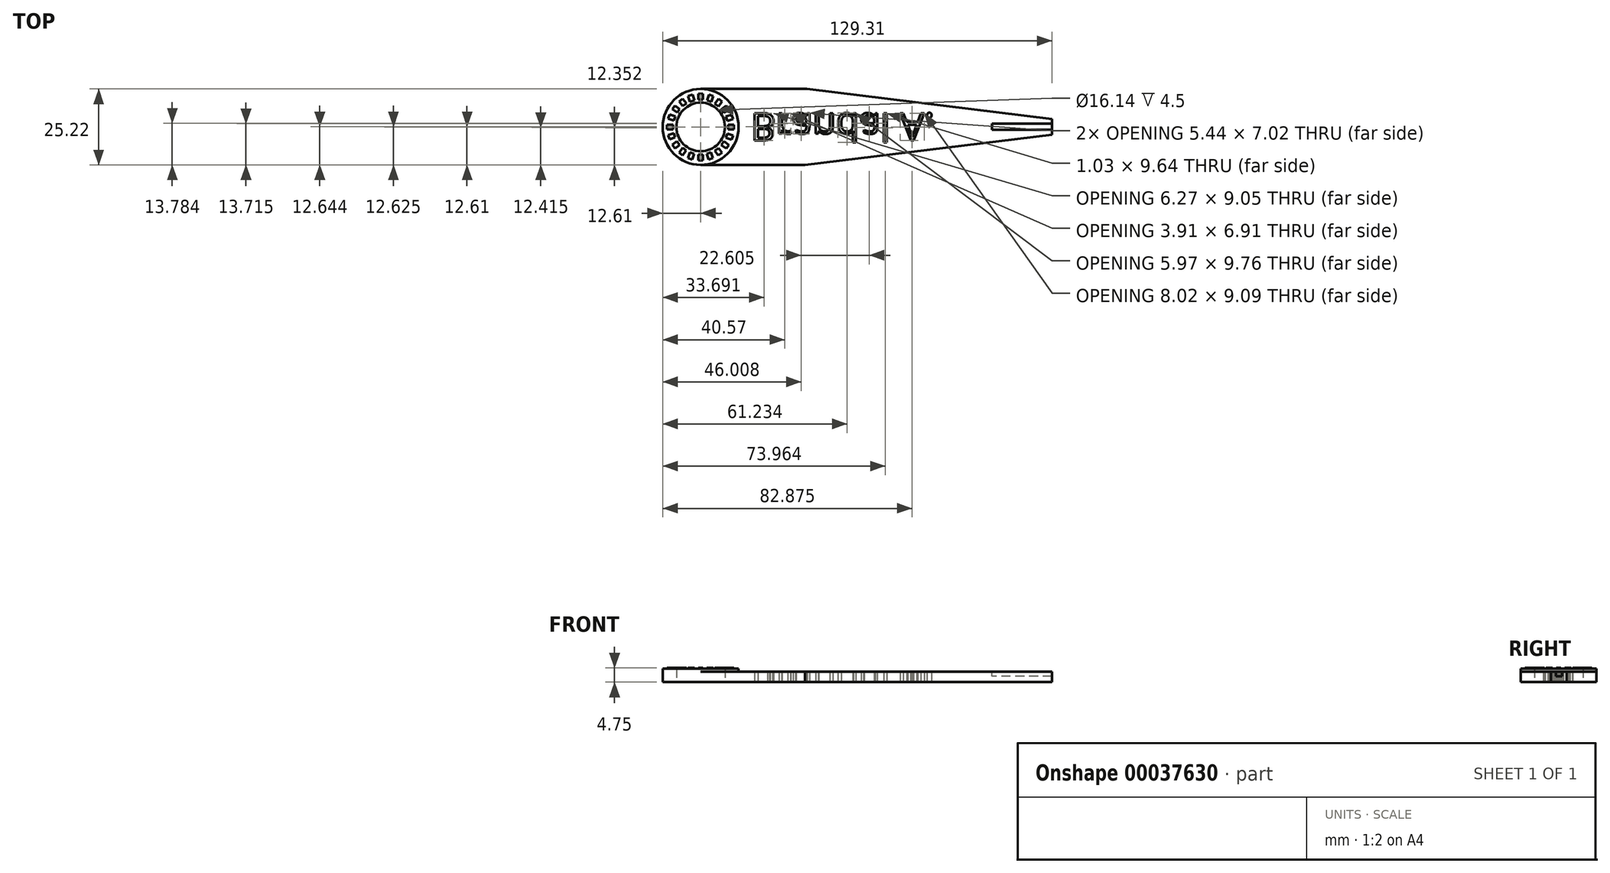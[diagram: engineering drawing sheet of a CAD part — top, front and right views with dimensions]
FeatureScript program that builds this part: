
annotation { "Feature Type Name" : "Feature", "Feature Type Description" : "" }
export const myFeature = defineFeature(function(context is Context, id is Id, definition is map)
    precondition{}
    {
        {
            var Q0;
            Q0=qCreatedBy(makeId("Top.planeOp"),FACE);
            var sketch = newSketch(context, id + "F0", { "sketchPlane" : qUnion([Q0])});
            skCircle(sketch, "E0", {"center": v(0, 0) * mm, "radius": 8.07 * mm});
            skArc(sketch, "E1", {"start": v(0, 12.6) * mm, "mid": v(-12.6, 0) * mm, "end": v(0, -12.6) * mm});
            skLineSegment(sketch, "E2", {"start": v(35.3, 12.6) * mm, "end": v(0, 12.6) * mm});
            skLineSegment(sketch, "E3", {"start": v(34.7, -12.6) * mm, "end": v(0, -12.6) * mm});
            skLineSegment(sketch, "E4", {"start": v(35.3, 12.6) * mm, "end": v(125.73, 12.6) * mm, "construction": true});
            skLineSegment(sketch, "E5", {"start": v(35.3, 12.6) * mm, "end": v(116.7, 2.62) * mm});
            skLineSegment(sketch, "E6.MirrorCS", {"start": v(34.7, -12.6) * mm, "end": v(116.7, -2.62) * mm});
            skLineSegment(sketch, "E7", {"start": v(116.7, 2.62) * mm, "end": v(116.7, -2.62) * mm});
            skSolve(sketch);
        }
        {
            var Q0;
            Q0=qSketchRegion(id+"F0",true);
            extrude(context, id + "F1", {"entities" : qUnion([Q0]), "depth" : 3.5 * mm});
        }
        {
            var Q0;
            Q0=makeQuery(id+"F1.opExtrude","CAP_FACE",FACE,{"disambiguationData":[OSD([sQuery(id+"F0.wireOp",EDGE,"E0"),sQuery(id+"F0.wireOp",EDGE,"E1"),sQuery(id+"F0.wireOp",EDGE,"E2"),sQuery(id+"F0.wireOp",EDGE,"E3"),sQuery(id+"F0.wireOp",EDGE,"E5"),sQuery(id+"F0.wireOp",EDGE,"E6.MirrorCS"),sQuery(id+"F0.wireOp",EDGE,"E7")])],"isStart":false});
            var sketch = newSketch(context, id + "F2", { "sketchPlane" : qUnion([Q0])});
            skCircle(sketch, "E8", {"center": v(0, 0) * mm, "radius": 8.07 * mm});
            skCircle(sketch, "E9", {"center": v(0, 0) * mm, "radius": 12.6 * mm});
            skSolve(sketch);
        }
        {
            var Q0;
            Q0=qSketchRegion(id+"F2",true);
            extrude(context, id + "F3", {"entities" : qUnion([Q0]), "operationType" : NewBodyOperationType.ADD, "depth" : 1 * mm});
        }
        {
            var Q0;
            Q0=makeQuery(id+"F3.opExtrude","CAP_FACE",FACE,{"disambiguationData":[OSD([sQuery(id+"F2.wireOp",EDGE,"E8"),sQuery(id+"F2.wireOp",EDGE,"E9")])],"isStart":false});
            var sketch = newSketch(context, id + "F4", { "sketchPlane" : qUnion([Q0])});
            skLineSegment(sketch, "E10.bottom", {"start": v(-0.75, 11.07) * mm, "end": v(0.75, 11.07) * mm});
            skLineSegment(sketch, "E10.top", {"start": v(-0.75, 9.07) * mm, "end": v(0.75, 9.07) * mm});
            skLineSegment(sketch, "E10.left", {"start": v(-0.75, 11.07) * mm, "end": v(-0.75, 9.07) * mm});
            skLineSegment(sketch, "E10.right", {"start": v(0.75, 11.07) * mm, "end": v(0.75, 9.07) * mm});
            skPoint(sketch, "E11", {"position": v(0, 8.07) * mm});
            skLineSegment(sketch, "E12.1.0", {"start": v(-4.14, 10.3) * mm, "end": v(-2.72, 10.77) * mm});
            skLineSegment(sketch, "E12.1.1", {"start": v(-4.14, 10.3) * mm, "end": v(-3.53, 8.4) * mm});
            skLineSegment(sketch, "E12.1.2", {"start": v(-3.53, 8.4) * mm, "end": v(-2.1, 8.87) * mm});
            skLineSegment(sketch, "E12.1.3", {"start": v(-2.72, 10.77) * mm, "end": v(-2.1, 8.87) * mm});
            skLineSegment(sketch, "E12.2.0", {"start": v(-7.14, 8.53) * mm, "end": v(-5.92, 9.4) * mm});
            skLineSegment(sketch, "E12.2.1", {"start": v(-7.14, 8.53) * mm, "end": v(-5.96, 6.9) * mm});
            skLineSegment(sketch, "E12.2.2", {"start": v(-5.96, 6.9) * mm, "end": v(-4.75, 7.8) * mm});
            skLineSegment(sketch, "E12.2.3", {"start": v(-5.92, 9.4) * mm, "end": v(-4.75, 7.8) * mm});
            skLineSegment(sketch, "E12.3.0", {"start": v(-9.43, 5.91) * mm, "end": v(-8.55, 7.13) * mm});
            skLineSegment(sketch, "E12.3.1", {"start": v(-9.43, 5.91) * mm, "end": v(-7.82, 4.74) * mm});
            skLineSegment(sketch, "E12.3.2", {"start": v(-7.82, 4.74) * mm, "end": v(-6.93, 5.95) * mm});
            skLineSegment(sketch, "E12.3.3", {"start": v(-8.55, 7.13) * mm, "end": v(-6.93, 5.95) * mm});
            skLineSegment(sketch, "E12.4.0", {"start": v(-10.8, 2.72) * mm, "end": v(-10.35, 4.14) * mm});
            skLineSegment(sketch, "E12.4.1", {"start": v(-10.8, 2.72) * mm, "end": v(-8.9, 2.1) * mm});
            skLineSegment(sketch, "E12.4.2", {"start": v(-8.9, 2.1) * mm, "end": v(-8.44, 3.52) * mm});
            skLineSegment(sketch, "E12.4.3", {"start": v(-10.35, 4.14) * mm, "end": v(-8.44, 3.52) * mm});
            skLineSegment(sketch, "E12.5.0", {"start": v(-11.13, -0.75) * mm, "end": v(-11.13, 0.75) * mm});
            skLineSegment(sketch, "E12.5.1", {"start": v(-11.13, -0.75) * mm, "end": v(-9.13, -0.75) * mm});
            skLineSegment(sketch, "E12.5.2", {"start": v(-9.13, -0.75) * mm, "end": v(-9.13, 0.75) * mm});
            skLineSegment(sketch, "E12.5.3", {"start": v(-11.13, 0.75) * mm, "end": v(-9.13, 0.75) * mm});
            skLineSegment(sketch, "E12.6.0", {"start": v(-10.36, -4.14) * mm, "end": v(-10.83, -2.72) * mm});
            skLineSegment(sketch, "E12.6.1", {"start": v(-10.36, -4.14) * mm, "end": v(-8.46, -3.53) * mm});
            skLineSegment(sketch, "E12.6.2", {"start": v(-8.46, -3.53) * mm, "end": v(-8.93, -2.1) * mm});
            skLineSegment(sketch, "E12.6.3", {"start": v(-10.83, -2.72) * mm, "end": v(-8.93, -2.1) * mm});
            skLineSegment(sketch, "E12.7.0", {"start": v(-8.59, -7.14) * mm, "end": v(-9.47, -5.92) * mm});
            skLineSegment(sketch, "E12.7.1", {"start": v(-8.59, -7.14) * mm, "end": v(-6.97, -5.96) * mm});
            skLineSegment(sketch, "E12.7.2", {"start": v(-6.97, -5.96) * mm, "end": v(-7.85, -4.75) * mm});
            skLineSegment(sketch, "E12.7.3", {"start": v(-9.47, -5.92) * mm, "end": v(-7.85, -4.75) * mm});
            skLineSegment(sketch, "E12.8.0", {"start": v(-5.97, -9.43) * mm, "end": v(-7.19, -8.55) * mm});
            skLineSegment(sketch, "E12.8.1", {"start": v(-5.97, -9.43) * mm, "end": v(-4.8, -7.82) * mm});
            skLineSegment(sketch, "E12.8.2", {"start": v(-4.8, -7.82) * mm, "end": v(-6.01, -6.93) * mm});
            skLineSegment(sketch, "E12.8.3", {"start": v(-7.19, -8.55) * mm, "end": v(-6.01, -6.93) * mm});
            skLineSegment(sketch, "E12.9.0", {"start": v(-2.78, -10.8) * mm, "end": v(-4.2, -10.35) * mm});
            skLineSegment(sketch, "E12.9.1", {"start": v(-2.78, -10.8) * mm, "end": v(-2.16, -8.9) * mm});
            skLineSegment(sketch, "E12.9.2", {"start": v(-2.16, -8.9) * mm, "end": v(-3.58, -8.44) * mm});
            skLineSegment(sketch, "E12.9.3", {"start": v(-4.2, -10.35) * mm, "end": v(-3.58, -8.44) * mm});
            skLineSegment(sketch, "E12.10.0", {"start": v(0.69, -11.13) * mm, "end": v(-0.81, -11.13) * mm});
            skLineSegment(sketch, "E12.10.1", {"start": v(0.69, -11.13) * mm, "end": v(0.69, -9.13) * mm});
            skLineSegment(sketch, "E12.10.2", {"start": v(0.69, -9.13) * mm, "end": v(-0.81, -9.13) * mm});
            skLineSegment(sketch, "E12.10.3", {"start": v(-0.81, -11.13) * mm, "end": v(-0.81, -9.13) * mm});
            skLineSegment(sketch, "E12.11.0", {"start": v(4.08, -10.36) * mm, "end": v(2.66, -10.83) * mm});
            skLineSegment(sketch, "E12.11.1", {"start": v(4.08, -10.36) * mm, "end": v(3.47, -8.46) * mm});
            skLineSegment(sketch, "E12.11.2", {"start": v(3.47, -8.46) * mm, "end": v(2.04, -8.93) * mm});
            skLineSegment(sketch, "E12.11.3", {"start": v(2.66, -10.83) * mm, "end": v(2.04, -8.93) * mm});
            skLineSegment(sketch, "E12.12.0", {"start": v(7.08, -8.59) * mm, "end": v(5.86, -9.47) * mm});
            skLineSegment(sketch, "E12.12.1", {"start": v(7.08, -8.59) * mm, "end": v(5.9, -6.97) * mm});
            skLineSegment(sketch, "E12.12.2", {"start": v(5.9, -6.97) * mm, "end": v(4.69, -7.85) * mm});
            skLineSegment(sketch, "E12.12.3", {"start": v(5.86, -9.47) * mm, "end": v(4.69, -7.85) * mm});
            skLineSegment(sketch, "E12.13.0", {"start": v(9.37, -5.97) * mm, "end": v(8.5, -7.19) * mm});
            skLineSegment(sketch, "E12.13.1", {"start": v(9.37, -5.97) * mm, "end": v(7.76, -4.8) * mm});
            skLineSegment(sketch, "E12.13.2", {"start": v(7.76, -4.8) * mm, "end": v(6.87, -6.01) * mm});
            skLineSegment(sketch, "E12.13.3", {"start": v(8.5, -7.19) * mm, "end": v(6.87, -6.01) * mm});
            skLineSegment(sketch, "E12.14.0", {"start": v(10.75, -2.78) * mm, "end": v(10.29, -4.2) * mm});
            skLineSegment(sketch, "E12.14.1", {"start": v(10.75, -2.78) * mm, "end": v(8.85, -2.16) * mm});
            skLineSegment(sketch, "E12.14.2", {"start": v(8.85, -2.16) * mm, "end": v(8.38, -3.58) * mm});
            skLineSegment(sketch, "E12.14.3", {"start": v(10.29, -4.2) * mm, "end": v(8.38, -3.58) * mm});
            skLineSegment(sketch, "E12.15.0", {"start": v(11.07, 0.69) * mm, "end": v(11.07, -0.81) * mm});
            skLineSegment(sketch, "E12.15.1", {"start": v(11.07, 0.69) * mm, "end": v(9.07, 0.69) * mm});
            skLineSegment(sketch, "E12.15.2", {"start": v(9.07, 0.69) * mm, "end": v(9.07, -0.81) * mm});
            skLineSegment(sketch, "E12.15.3", {"start": v(11.07, -0.81) * mm, "end": v(9.07, -0.81) * mm});
            skLineSegment(sketch, "E12.16.0", {"start": v(10.3, 4.08) * mm, "end": v(10.77, 2.66) * mm});
            skLineSegment(sketch, "E12.16.1", {"start": v(10.3, 4.08) * mm, "end": v(8.4, 3.47) * mm});
            skLineSegment(sketch, "E12.16.2", {"start": v(8.4, 3.47) * mm, "end": v(8.87, 2.04) * mm});
            skLineSegment(sketch, "E12.16.3", {"start": v(10.77, 2.66) * mm, "end": v(8.87, 2.04) * mm});
            skLineSegment(sketch, "E12.17.0", {"start": v(8.53, 7.08) * mm, "end": v(9.4, 5.86) * mm});
            skLineSegment(sketch, "E12.17.1", {"start": v(8.53, 7.08) * mm, "end": v(6.9, 5.9) * mm});
            skLineSegment(sketch, "E12.17.2", {"start": v(6.9, 5.9) * mm, "end": v(7.8, 4.69) * mm});
            skLineSegment(sketch, "E12.17.3", {"start": v(9.4, 5.86) * mm, "end": v(7.8, 4.69) * mm});
            skLineSegment(sketch, "E12.18.0", {"start": v(5.91, 9.37) * mm, "end": v(7.13, 8.5) * mm});
            skLineSegment(sketch, "E12.18.1", {"start": v(5.91, 9.37) * mm, "end": v(4.74, 7.76) * mm});
            skLineSegment(sketch, "E12.18.2", {"start": v(4.74, 7.76) * mm, "end": v(5.95, 6.87) * mm});
            skLineSegment(sketch, "E12.18.3", {"start": v(7.13, 8.5) * mm, "end": v(5.95, 6.87) * mm});
            skLineSegment(sketch, "E12.19.0", {"start": v(2.72, 10.75) * mm, "end": v(4.14, 10.29) * mm});
            skLineSegment(sketch, "E12.19.1", {"start": v(2.72, 10.75) * mm, "end": v(2.1, 8.85) * mm});
            skLineSegment(sketch, "E12.19.2", {"start": v(2.1, 8.85) * mm, "end": v(3.52, 8.38) * mm});
            skLineSegment(sketch, "E12.19.3", {"start": v(4.14, 10.29) * mm, "end": v(3.52, 8.38) * mm});
            skPoint(sketch, "E12.center", {"position": v(-0.03, -0.03) * mm});
            skSolve(sketch);
        }
        {
            var Q0;
            Q0=qSketchRegion(id+"F4",true);
            extrude(context, id + "F5", {"entities" : qUnion([Q0]), "operationType" : NewBodyOperationType.ADD, "depth" : .25 * mm});
        }
        {
            var Q0;
            Q0=makeQuery(id+"F1.opExtrude","CAP_FACE",FACE,{"disambiguationData":[OSD([sQuery(id+"F0.wireOp",EDGE,"E0"),sQuery(id+"F0.wireOp",EDGE,"E1"),sQuery(id+"F0.wireOp",EDGE,"E2"),sQuery(id+"F0.wireOp",EDGE,"E3"),sQuery(id+"F0.wireOp",EDGE,"E5"),sQuery(id+"F0.wireOp",EDGE,"E6.MirrorCS"),sQuery(id+"F0.wireOp",EDGE,"E7")])],"isStart":false});
            var sketch = newSketch(context, id + "F6", { "sketchPlane" : qUnion([Q0])});
            skLineSegment(sketch, "E13.bottom", {"start": v(116.7, 1.12) * mm, "end": v(96.7, 1.12) * mm});
            skLineSegment(sketch, "E13.top", {"start": v(116.7, -0.88) * mm, "end": v(96.7, -0.88) * mm});
            skLineSegment(sketch, "E13.left", {"start": v(116.7, 1.12) * mm, "end": v(116.7, -0.88) * mm});
            skLineSegment(sketch, "E13.right", {"start": v(96.7, 1.12) * mm, "end": v(96.7, -0.88) * mm});
            skSolve(sketch);
        }
        {
            var Q0;
            Q0=makeQuery(id+"F6.imprint","IMPRINT",FACE,{"disambiguationData":[TD([[makeQuery(id+"F6.imprint","IMPRINT",EDGE,{"derivedFrom":sQuery(id+"F6.wireOp",EDGE,"E13.bottom")}),1.0]])]});
            extrude(context, id + "F7", {"entities" : qUnion([Q0]), "operationType" : NewBodyOperationType.REMOVE, "oppositeDirection" : true, "depth" : 1.5 * mm});
        }
        {
            var Q0;
            Q0=makeQuery(id+"F1.opExtrude","CAP_EDGE",EDGE,{"disambiguationData":[OSD([sQuery(id+"F0.wireOp",EDGE,"E3")])],"isStart":true});
            cPlane(context, id + "F8", {"entities" : qUnion([Q0]), "cplaneType" : CPlaneType.LINE_ANGLE, "offset" : 150 * mm, "angle" : 270 * degree, "width" : 150 * mm, "height" : 150 * mm});
        }
        {
            var Q0;
            Q0=qCreatedBy(id+"F8.planeOp",FACE);
            var sketch = newSketch(context, id + "F9", { "sketchPlane" : qUnion([Q0])});
            skLineSegment(sketch, "E14", {"start": v(0, 0) * mm, "end": v(33.4, 0) * mm, "construction": true});
            skPoint(sketch, "E15", {"position": v(16.7, 0) * mm});
            skText(sketch, "E16", { "text": "Brandal A.", "fontName": "OpenSans-Regular.ttf"});
            const initialGuessF9  = {"E16": [0.0167, -0.00456, 1, 0, 0.00913]};
            skSetInitialGuess(sketch, initialGuessF9);
            skSolve(sketch);
        }
        {
            var Q0;
            Q0=qSketchRegion(id+"F9",true);
            extrude(context, id + "F10", {"entities" : qUnion([Q0]), "operationType" : NewBodyOperationType.REMOVE, "endBound" : BoundingType.THROUGH_ALL, "oppositeDirection" : true, "depth" : 25 * mm});
        }
    });
